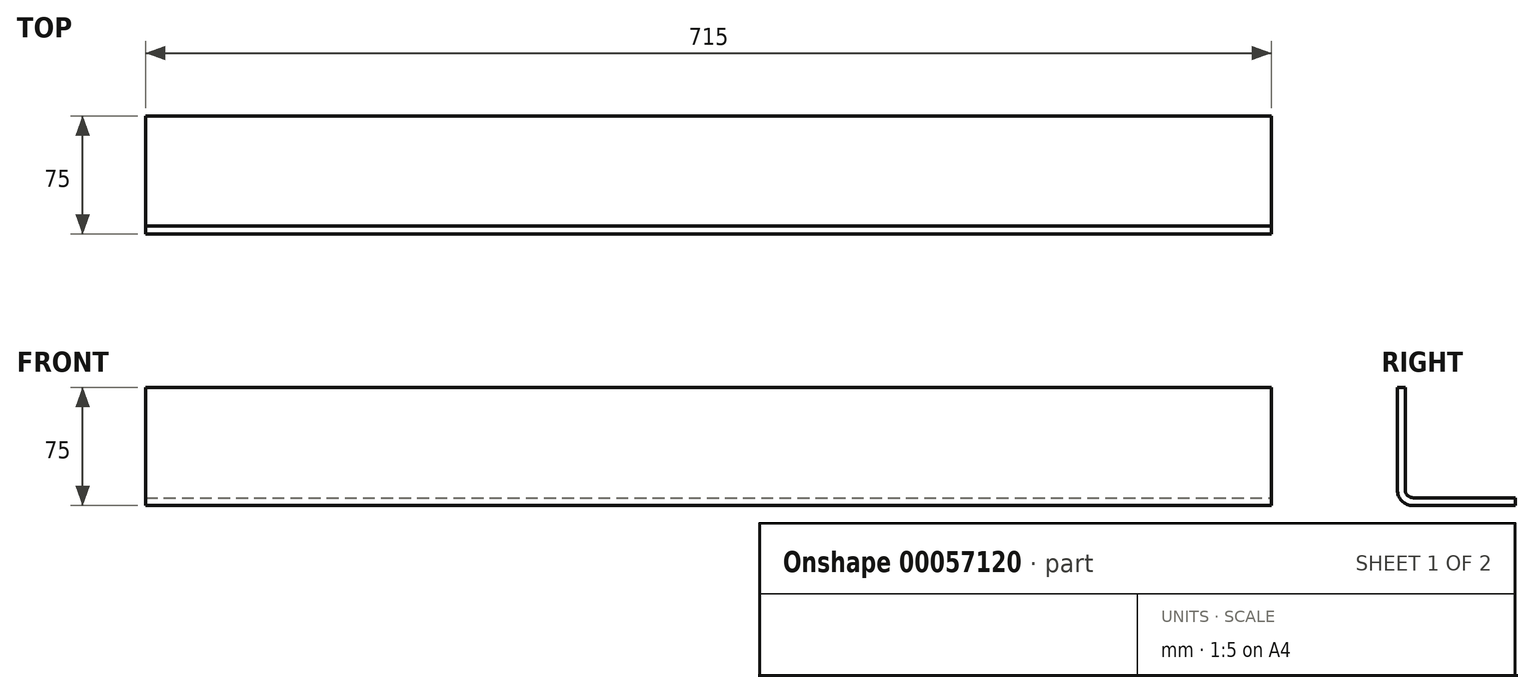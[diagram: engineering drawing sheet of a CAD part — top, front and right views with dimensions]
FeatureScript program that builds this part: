
annotation { "Feature Type Name" : "Feature", "Feature Type Description" : "" }
export const myFeature = defineFeature(function(context is Context, id is Id, definition is map)
    precondition{}
    {
        {
            var Q0;
            Q0=qCreatedBy(makeId("Front.planeOp"),FACE);
            var sketch = newSketch(context, id + "F0", { "sketchPlane" : qUnion([Q0])});
            skLineSegment(sketch, "E0.bottom", {"start": v(-715, 75) * mm, "end": v(0, 75) * mm});
            skLineSegment(sketch, "E0.top", {"start": v(-715, 0) * mm, "end": v(0, 0) * mm});
            skLineSegment(sketch, "E0.left", {"start": v(-715, 75) * mm, "end": v(-715, 0) * mm});
            skLineSegment(sketch, "E0.right", {"start": v(0, 75) * mm, "end": v(0, 0) * mm});
            skSolve(sketch);
        }
        {
            var Q0;
            Q0 = qSketchRegion(id + "F0", true);
            extrude(context, id + "F1", {"entities" : qUnion([Q0]), "oppositeDirection" : true, "depth" : 75 * mm});
        }
        {
            var Q0;
            Q0=makeQuery(id+"F1.opExtrude","CAP_EDGE",EDGE,{"disambiguationData":[OSD([sQuery(id+"F0.wireOp",EDGE,"E0.top")])],"isStart":true});
            fillet(context, id + "F2", {"entities" : qUnion([Q0]), "radius" : 10 * mm, "tangentPropagation" : true, "allowEdgeOverflow" : false});
        }
        {
            var Q0;
            Q0=makeQuery(id+"F1.opExtrude","SWEPT_FACE",FACE,{"disambiguationData":[OSD([sQuery(id+"F0.wireOp",EDGE,"E0.bottom")])]});
            var Q1;
            Q1=makeQuery(id+"F1.opExtrude","CAP_FACE",FACE,{"disambiguationData":[OSD([sQuery(id+"F0.wireOp",EDGE,"E0.bottom"),sQuery(id+"F0.wireOp",EDGE,"E0.top"),sQuery(id+"F0.wireOp",EDGE,"E0.left"),sQuery(id+"F0.wireOp",EDGE,"E0.right")])],"isStart":false});
            var Q2;
            Q2=makeQuery(id+"F1.opExtrude","SWEPT_FACE",FACE,{"disambiguationData":[OSD([sQuery(id+"F0.wireOp",EDGE,"E0.right")])]});
            var Q3;
            Q3=makeQuery(id+"F1.opExtrude","SWEPT_FACE",FACE,{"disambiguationData":[OSD([sQuery(id+"F0.wireOp",EDGE,"E0.left")])]});
            shell(context, id + "F3", {"entities" : qUnion([Q0, Q1, Q2, Q3]), "thickness" : 5 * mm});
        }
    });
